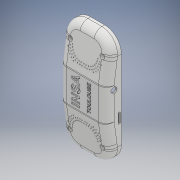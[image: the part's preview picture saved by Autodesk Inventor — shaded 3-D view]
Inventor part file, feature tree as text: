
AUTODESK INVENTOR PART (.ipt)
format: ipt  version: 2019 (Build 230136000, 136)  size: 1,051,648 bytes
history: native  units: mm
features: sketch x15, extrude x14, chamfer x2, fillet x2, shell x1, other x1
ambient origin geometry x8: Origin, YZ Plane, XZ Plane, XY Plane, X Axis, Y Axis, Z Axis, Center Point
bodies: Solide1 (feature_tree)
feature tree (35):
  extrude  "Extrusion1"  Depth=200.0mm
  extrude  "Extrusion11"  Depth=85.0mm
  chamfer  "Chanfrein1"  Distance=42.5mm
  chamfer  "Chanfrein2"  Distance=100.0mm
  fillet  "Congé3"  Radius=28.0mm
  fillet  "Congé4"  Radius=10.0mm
  shell  "Coque1"  Thickness=10.0mm
  extrude  "Extrusion2"  Depth=30.0mm
  extrude  "Extrusion3"  Depth=14.0mm
  extrude  "Extrusion4"  Depth=2.5mm
  extrude  "Extrusion5"  Depth=2.5mm TaperAngle=0.0deg
  extrude  "Extrusion6"  Depth=108.0mm
  extrude  "Extrusion7"  Depth=70.0mm
  extrude  "Extrusion8"  Depth=35.0mm
  extrude  "Extrusion9"  Depth=54.0mm
  extrude  "Extrusion12"  Depth=10.0mm
  extrude  "Extrusion13"  Depth=10.0mm
  extrude  "Extrusion14"  Depth=10.0mm
  other  "Gravure1"
  extrude  "Extrusion15"  Depth=10.0mm
  sketch  "Esquisse1"
  sketch  "Esquisse3"
  sketch  "Esquisse4"
  sketch  "Esquisse5"
  sketch  "Esquisse6"
  sketch  "Esquisse7"
  sketch  "Esquisse8"
  sketch  "Esquisse9"
  sketch  "Esquisse10"
  sketch  "Esquisse11"
  sketch  "Esquisse14"
  sketch  "Esquisse15"
  sketch  "Esquisse16"
  sketch  "Esquisse17"
  sketch  "Esquisse18"
